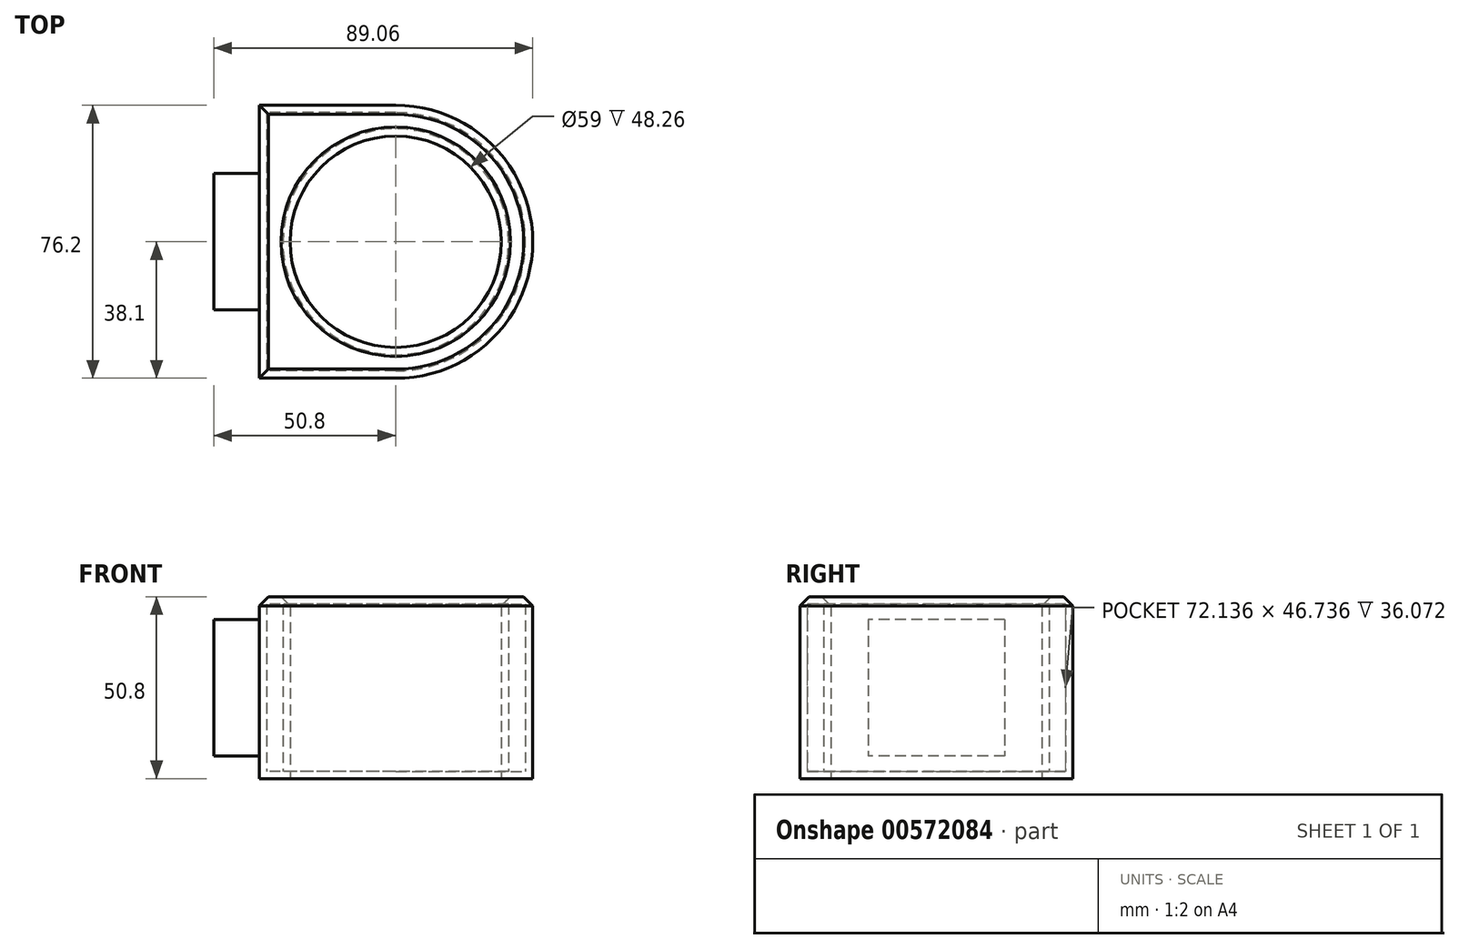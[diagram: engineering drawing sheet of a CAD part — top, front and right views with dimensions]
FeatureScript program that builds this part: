
annotation { "Feature Type Name" : "Feature", "Feature Type Description" : "" }
export const myFeature = defineFeature(function(context is Context, id is Id, definition is map)
    precondition{}
    {
        {
            var Q0;
            Q0=qCreatedBy(makeId("Top.planeOp"),FACE);
            var sketch = newSketch(context, id + "F0", { "sketchPlane" : qUnion([Q0])});
            skLineSegment(sketch, "E0.bottom", {"start": v(0.33, 38.1) * mm, "end": v(-38.1, 38.1) * mm});
            skLineSegment(sketch, "E0.top", {"start": v(0.33, -38.1) * mm, "end": v(-38.1, -38.1) * mm});
            skLineSegment(sketch, "E0.right", {"start": v(-38.1, 38.1) * mm, "end": v(-38.1, -38.1) * mm});
            skPoint(sketch, "E0.middle", {"position": v(0, 0) * mm});
            skCircle(sketch, "E1", {"center": v(0, 0) * mm, "radius": 29.5 * mm});
            skArc(sketch, "E2", {"start": v(0, -38.1) * mm, "mid": v(38.26, 0) * mm, "end": v(0, 38.1) * mm});
            skPoint(sketch, "E3.orphan", {"position": v(38.1, 38.1) * mm});
            skPoint(sketch, "E4.orphan", {"position": v(38.1, -38.1) * mm});
            skSolve(sketch);
        }
        {
            var Q0;
            Q0 = qSketchRegion(id + "F0", true);
            extrude(context, id + "F1", {"entities" : qUnion([Q0]), "depth" : 50.8 * mm, "offsetDistance" : 25.4 * mm});
        }
        {
            var Q0;
            Q0=makeQuery(id+"F1.opExtrude","SWEPT_FACE",FACE,{"disambiguationData":[OSD([sQuery(id+"F0.wireOp",EDGE,"E0.right")])]});
            var sketch = newSketch(context, id + "F2", { "sketchPlane" : qUnion([Q0])});
            skLineSegment(sketch, "E5.bottom", {"start": v(-19.05, 44.45) * mm, "end": v(19.05, 44.45) * mm});
            skLineSegment(sketch, "E5.top", {"start": v(-19.05, 6.35) * mm, "end": v(19.05, 6.35) * mm});
            skLineSegment(sketch, "E5.left", {"start": v(-19.05, 44.45) * mm, "end": v(-19.05, 6.35) * mm});
            skLineSegment(sketch, "E5.right", {"start": v(19.05, 44.45) * mm, "end": v(19.05, 6.35) * mm});
            skPoint(sketch, "E5.middle", {"position": v(0, 25.4) * mm});
            skSolve(sketch);
        }
        {
            var Q0;
            Q0=makeQuery(id+"F1.opExtrude","SWEPT_FACE",FACE,{"disambiguationData":[OSD([sQuery(id+"F0.wireOp",EDGE,"E0.left")])]});
            var Q1;
            Q1=makeQuery(id+"F1.opExtrude","SWEPT_BODY",BODY,{"disambiguationData":[OSD([sQuery(id+"F0.wireOp",EDGE,"E0.bottom"),sQuery(id+"F0.wireOp",EDGE,"E0.top"),sQuery(id+"F0.wireOp",EDGE,"E0.left"),sQuery(id+"F0.wireOp",EDGE,"E0.right"),sQuery(id+"F0.wireOp",EDGE,"E1")])]});
            shell(context, id + "F3", {"isHollow" : true, "entities" : qUnion([Q0]), "parts" : qUnion([Q1]), "thickness" : 2.03 * mm});
        }
        {
            var Q0;
            Q0 = qSketchRegion(id + "F2", true);
            extrude(context, id + "F4", {"entities" : qUnion([Q0]), "operationType" : NewBodyOperationType.ADD, "depth" : 12.7 * mm, "offsetDistance" : 25.4 * mm});
        }
        {
            var Q0;
            Q0=makeQuery(id+"F1.opExtrude","CAP_FACE",FACE,{"disambiguationData":[OSD([sQuery(id+"F0.wireOp",EDGE,"E0.bottom"),sQuery(id+"F0.wireOp",EDGE,"E0.top"),sQuery(id+"F0.wireOp",EDGE,"E0.right"),sQuery(id+"F0.wireOp",EDGE,"E1"),sQuery(id+"F0.wireOp",EDGE,"E2")])],"isStart":false});
            chamfer(context, id + "F5", {"entities" : qUnion([Q0]), "width" : 2.54 * mm, "tangentPropagation" : true});
        }
    });
